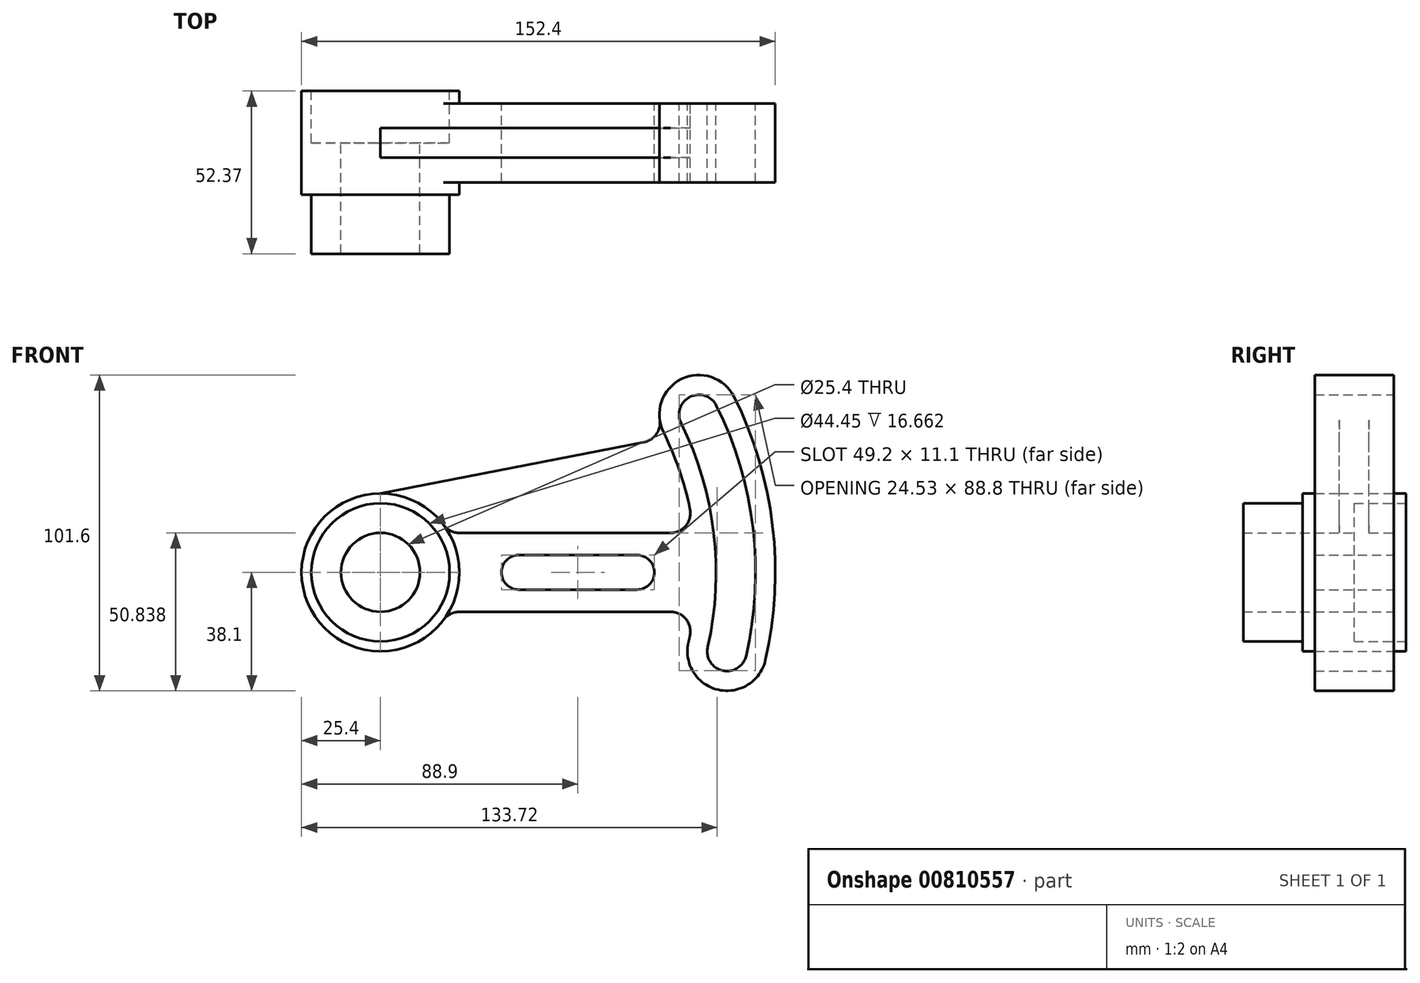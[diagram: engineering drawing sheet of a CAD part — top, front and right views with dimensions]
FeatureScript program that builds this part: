
annotation { "Feature Type Name" : "Feature", "Feature Type Description" : "" }
export const myFeature = defineFeature(function(context is Context, id is Id, definition is map)
    precondition{}
    {
        {
            var Q0;
            Q0=qCreatedBy(makeId("Front.planeOp"),FACE);
            var sketch = newSketch(context, id + "F0", { "sketchPlane" : qUnion([Q0])});
            skCircle(sketch, "E0", {"center": v(0, 0) * mm, "radius": 12.7 * mm});
            skCircle(sketch, "E1", {"center": v(0, 0) * mm, "radius": 22.23 * mm});
            skCircle(sketch, "E2", {"center": v(0, 0) * mm, "radius": 25.4 * mm});
            skLineSegment(sketch, "E3.bottom", {"start": v(25.4, 12.7) * mm, "end": v(93.33, 12.7) * mm});
            skLineSegment(sketch, "E3.top", {"start": v(25.4, -12.7) * mm, "end": v(93.33, -12.7) * mm});
            skLineSegment(sketch, "E3.left", {"start": v(0, 12.7) * mm, "end": v(0, -12.7) * mm});
            skArc(sketch, "E4", {"start": v(113.77, 56.44) * mm, "mid": v(96.75, 62.18) * mm, "end": v(91.01, 45.16) * mm});
            skArc(sketch, "E5", {"start": v(99.06, -22.58) * mm, "mid": v(108.62, -37.78) * mm, "end": v(123.82, -28.22) * mm});
            skArc(sketch, "E6", {"start": v(108.08, 53.62) * mm, "mid": v(99.57, 56.49) * mm, "end": v(96.7, 47.98) * mm});
            skArc(sketch, "E7", {"start": v(105.25, -23.99) * mm, "mid": v(110.03, -31.6) * mm, "end": v(117.63, -26.81) * mm});
            skArc(sketch, "E8", {"start": v(25.4, -12.7) * mm, "mid": v(22.56, -13.37) * mm, "end": v(20.32, -15.24) * mm});
            skArc(sketch, "E9", {"start": v(20.32, 15.24) * mm, "mid": v(22.56, 13.37) * mm, "end": v(25.4, 12.7) * mm});
            skArc(sketch, "E10", {"start": v(44.45, 5.55) * mm, "mid": v(38.9, 0) * mm, "end": v(44.45, -5.55) * mm});
            skArc(sketch, "E11", {"start": v(82.55, -5.55) * mm, "mid": v(88.1, 0) * mm, "end": v(82.55, 5.55) * mm});
            skLineSegment(sketch, "E12", {"start": v(44.45, -5.55) * mm, "end": v(82.55, -5.55) * mm});
            skLineSegment(sketch, "E13", {"start": v(44.45, 5.55) * mm, "end": v(82.55, 5.55) * mm});
            skArc(sketch, "E14", {"start": v(105.25, -23.99) * mm, "mid": v(107.2, 12.73) * mm, "end": v(96.7, 47.98) * mm});
            skArc(sketch, "E15", {"start": v(117.63, -26.81) * mm, "mid": v(119.8, 14.23) * mm, "end": v(108.08, 53.62) * mm});
            skArc(sketch, "E16", {"start": v(123.82, -28.22) * mm, "mid": v(126.11, 14.98) * mm, "end": v(113.77, 56.44) * mm});
            skArc(sketch, "E17", {"start": v(99.06, -22.58) * mm, "mid": v(99.3, -21.45) * mm, "end": v(99.55, -20.32) * mm});
            skPoint(sketch, "E18.orphan", {"position": v(125.14, 0) * mm});
            skPoint(sketch, "E19.orphan", {"position": v(125.14, 12.7) * mm});
            skPoint(sketch, "E20.trimOffspring.end.orphan", {"position": v(125.14, -12.7) * mm});
            skArc(sketch, "E21", {"start": v(93.33, 12.7) * mm, "mid": v(98.24, 15.03) * mm, "end": v(99.55, 20.32) * mm});
            skArc(sketch, "E22", {"start": v(99.55, -20.32) * mm, "mid": v(98.24, -15.03) * mm, "end": v(93.33, -12.7) * mm});
            skArc(sketch, "E23.trimOffspring", {"start": v(99.55, 20.32) * mm, "mid": v(96.09, 33.01) * mm, "end": v(91.01, 45.16) * mm});
            skLineSegment(sketch, "E24", {"start": v(0, 25.4) * mm, "end": v(84.74, 41.87) * mm});
            skArc(sketch, "E25", {"start": v(84.74, 41.87) * mm, "mid": v(88.7, 44.42) * mm, "end": v(89.82, 49) * mm});
            skPoint(sketch, "E26.trimOffspring.end.orphan", {"position": v(145.2, 53.62) * mm});
            skSolve(sketch);
        }
        {
            var Q0;
            Q0=makeQuery(id+"F0.imprint","IMPRINT",FACE,{"disambiguationData":[TD([[makeQuery(id+"F0.imprint","IMPRINT",EDGE,{"derivedFrom":sQuery(id+"F0.wireOp",EDGE,"E1")}),1.0]])]});
            extrude(context, id + "F1", {"entities" : qUnion([Q0]), "depth" : 35.7 * mm, "offsetDistance" : 25.4 * mm});
        }
        {
            var Q0;
            Q0=makeQuery(id+"F0.imprint","IMPRINT",FACE,{"disambiguationData":[TD([[makeQuery(id+"F0.imprint","IMPRINT",EDGE,{"derivedFrom":sQuery(id+"F0.wireOp",EDGE,"E1")}),-1.0]])]});
            extrude(context, id + "F2", {"entities" : qUnion([Q0]), "operationType" : NewBodyOperationType.ADD, "endBound" : BoundingType.SYMMETRIC, "depth" : 33.32 * mm, "offsetDistance" : 25.4 * mm});
        }
        {
            var Q0;
            Q0=makeQuery(id+"F0.imprint","IMPRINT",FACE,{"disambiguationData":[TD([[makeQuery(id+"F0.imprint","IMPRINT",EDGE,{"derivedFrom":sQuery(id+"F0.wireOp",EDGE,"E3.bottom")}),1.0]])]});
            extrude(context, id + "F3", {"entities" : qUnion([Q0]), "operationType" : NewBodyOperationType.ADD, "endBound" : BoundingType.SYMMETRIC, "depth" : 9.52 * mm, "offsetDistance" : 25.4 * mm});
        }
        {
            var Q0;
            Q0=makeQuery(id+"F0.imprint","IMPRINT",FACE,{"disambiguationData":[TD([[makeQuery(id+"F0.imprint","IMPRINT",EDGE,{"derivedFrom":sQuery(id+"F0.wireOp",EDGE,"E3.bottom")}),-1.0]])]});
            extrude(context, id + "F4", {"entities" : qUnion([Q0]), "operationType" : NewBodyOperationType.ADD, "endBound" : BoundingType.SYMMETRIC, "depth" : 25.37 * mm, "offsetDistance" : 25.4 * mm});
        }
    });
